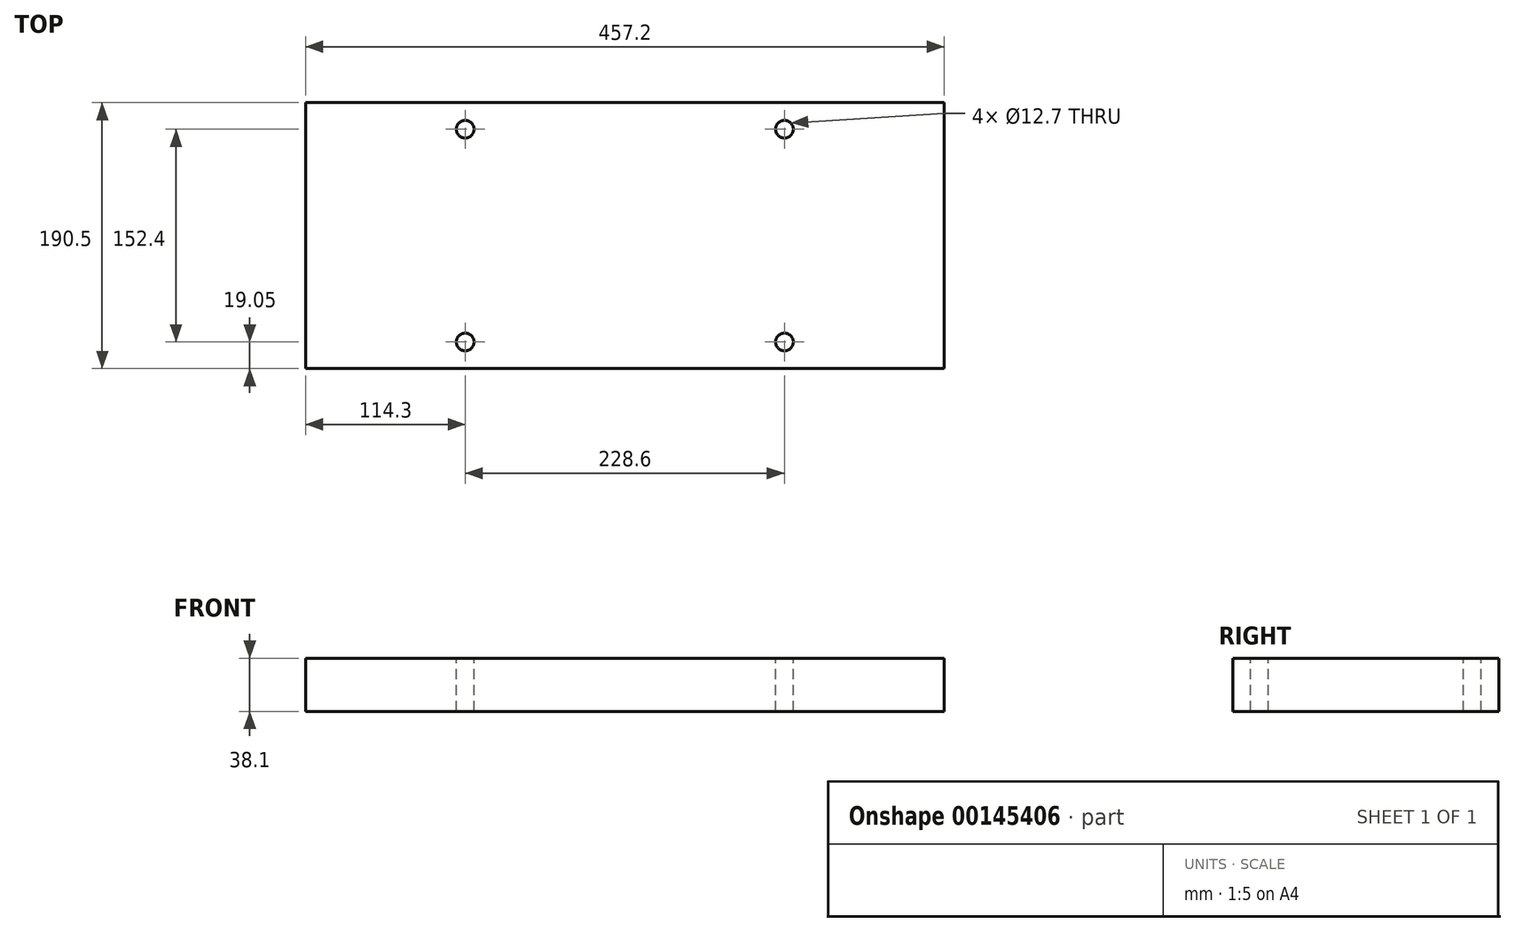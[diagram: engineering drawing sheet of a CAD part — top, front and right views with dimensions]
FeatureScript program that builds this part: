
annotation { "Feature Type Name" : "Feature", "Feature Type Description" : "" }
export const myFeature = defineFeature(function(context is Context, id is Id, definition is map)
    precondition{}
    {
        {
            var Q0;
            Q0=qCreatedBy(makeId("Front.planeOp"),FACE);
            var sketch = newSketch(context, id + "F0", { "sketchPlane" : qUnion([Q0])});
            skLineSegment(sketch, "E0.bottom", {"start": v(-228.6, 19.05) * mm, "end": v(228.6, 19.05) * mm});
            skLineSegment(sketch, "E0.top", {"start": v(-228.6, -19.05) * mm, "end": v(228.6, -19.05) * mm});
            skLineSegment(sketch, "E0.left", {"start": v(-228.6, 19.05) * mm, "end": v(-228.6, -19.05) * mm});
            skLineSegment(sketch, "E0.right", {"start": v(228.6, 19.05) * mm, "end": v(228.6, -19.05) * mm});
            skPoint(sketch, "E0.middle", {"position": v(0, 0) * mm});
            skSolve(sketch);
        }
        {
            var Q0;
            Q0 = qSketchRegion(id + "F0", true);
            extrude(context, id + "F1", {"entities" : qUnion([Q0]), "endBound" : BoundingType.SYMMETRIC, "depth" : 190.5 * mm});
        }
        {
            var Q0;
            Q0=makeQuery(id+"F1.opExtrude","SWEPT_BODY",BODY,{"disambiguationData":[OSD([sQuery(id+"F0.wireOp",EDGE,"E0.bottom"),sQuery(id+"F0.wireOp",EDGE,"E0.top"),sQuery(id+"F0.wireOp",EDGE,"E0.left"),sQuery(id+"F0.wireOp",EDGE,"E0.right")])]});
            transform(context, id + "F2", {"entities" : qUnion([Q0]), "transformType" : TransformType.TRANSLATION_3D, "dx" : 0 * mm, "dy" : 0 * mm, "dz" : 152.4 * mm, "makeCopy" : true});
        }
        {
            var Q0;
            Q0=makeQuery(id+"F2.opPattern","COPY",FACE,{"derivedFrom":makeQuery(id+"F1.opExtrude","SWEPT_FACE",FACE,{"disambiguationData":[OSD([sQuery(id+"F0.wireOp",EDGE,"E0.bottom")])]}),"instanceName":"1"});
            var sketch = newSketch(context, id + "F3", { "sketchPlane" : qUnion([Q0])});
            skPoint(sketch, "E1", {"position": v(114.3, 76.2) * mm});
            skPoint(sketch, "E2", {"position": v(114.3, -76.2) * mm});
            skPoint(sketch, "E3", {"position": v(-114.3, 76.2) * mm});
            skPoint(sketch, "E4", {"position": v(-114.3, -76.2) * mm});
            skSolve(sketch);
        }
        {
            var Q0;
            Q0=sQuery(id+"F3.wireOp",VERTEX,"4ecf7e5d-f871-4dc4-9d11-71fa30564b7e");
            var Q1;
            Q1=sQuery(id+"F3.wireOp",VERTEX,"E3");
            var Q2;
            Q2=makeQuery(id+"F2.opPattern","COPY",BODY,{"derivedFrom":makeQuery(id+"F1.opExtrude","SWEPT_BODY",BODY,{"disambiguationData":[OSD([sQuery(id+"F0.wireOp",EDGE,"E0.bottom"),sQuery(id+"F0.wireOp",EDGE,"E0.top"),sQuery(id+"F0.wireOp",EDGE,"E0.left"),sQuery(id+"F0.wireOp",EDGE,"E0.right")])]}),"instanceName":"1"});
            var Q3;
            Q3=makeQuery(id+"F1.opExtrude","SWEPT_BODY",BODY,{"disambiguationData":[OSD([sQuery(id+"F0.wireOp",EDGE,"E0.bottom"),sQuery(id+"F0.wireOp",EDGE,"E0.top"),sQuery(id+"F0.wireOp",EDGE,"E0.left"),sQuery(id+"F0.wireOp",EDGE,"E0.right")])]});
            hole(context, id + "F4", {"style" : HoleStyle.SIMPLE, "endStyle" : HoleEndStyle.BLIND, "holeDiameter" : 12.7 * mm, "holeDepth" : 609.6 * mm, "locations" : qUnion([Q0, Q1]), "scope" : qUnion([Q2, Q3])});
        }
        {
            var Q0;
            Q0=sQuery(id+"F3.wireOp",VERTEX,"1e3262fc-aa90-4388-9655-f59d1800e4ad");
            var Q1;
            Q1=sQuery(id+"F3.wireOp",VERTEX,"E1");
            var Q2;
            Q2=makeQuery(id+"F2.opPattern","COPY",BODY,{"derivedFrom":makeQuery(id+"F1.opExtrude","SWEPT_BODY",BODY,{"disambiguationData":[OSD([sQuery(id+"F0.wireOp",EDGE,"E0.bottom"),sQuery(id+"F0.wireOp",EDGE,"E0.top"),sQuery(id+"F0.wireOp",EDGE,"E0.left"),sQuery(id+"F0.wireOp",EDGE,"E0.right")])]}),"instanceName":"1"});
            var Q3;
            Q3=makeQuery(id+"F1.opExtrude","SWEPT_BODY",BODY,{"disambiguationData":[OSD([sQuery(id+"F0.wireOp",EDGE,"E0.bottom"),sQuery(id+"F0.wireOp",EDGE,"E0.top"),sQuery(id+"F0.wireOp",EDGE,"E0.left"),sQuery(id+"F0.wireOp",EDGE,"E0.right")])]});
            hole(context, id + "F5", {"style" : HoleStyle.SIMPLE, "endStyle" : HoleEndStyle.BLIND, "holeDiameter" : 12.7 * mm, "holeDepth" : 609.6 * mm, "locations" : qUnion([Q0, Q1]), "scope" : qUnion([Q2, Q3])});
        }
        {
            var Q0;
            Q0=sQuery(id+"F3.wireOp",VERTEX,"c1e96b3d-2616-42c4-94e8-07fb85a00044");
            var Q1;
            Q1=sQuery(id+"F3.wireOp",VERTEX,"E4");
            var Q2;
            Q2=makeQuery(id+"F2.opPattern","COPY",BODY,{"derivedFrom":makeQuery(id+"F1.opExtrude","SWEPT_BODY",BODY,{"disambiguationData":[OSD([sQuery(id+"F0.wireOp",EDGE,"E0.bottom"),sQuery(id+"F0.wireOp",EDGE,"E0.top"),sQuery(id+"F0.wireOp",EDGE,"E0.left"),sQuery(id+"F0.wireOp",EDGE,"E0.right")])]}),"instanceName":"1"});
            var Q3;
            Q3=makeQuery(id+"F1.opExtrude","SWEPT_BODY",BODY,{"disambiguationData":[OSD([sQuery(id+"F0.wireOp",EDGE,"E0.bottom"),sQuery(id+"F0.wireOp",EDGE,"E0.top"),sQuery(id+"F0.wireOp",EDGE,"E0.left"),sQuery(id+"F0.wireOp",EDGE,"E0.right")])]});
            hole(context, id + "F6", {"style" : HoleStyle.SIMPLE, "endStyle" : HoleEndStyle.BLIND, "holeDiameter" : 12.7 * mm, "holeDepth" : 609.6 * mm, "locations" : qUnion([Q0, Q1]), "scope" : qUnion([Q2, Q3])});
        }
        {
            var Q0;
            Q0=sQuery(id+"F3.wireOp",VERTEX,"f6763203-d3ba-4051-b323-57933851997e");
            var Q1;
            Q1=sQuery(id+"F3.wireOp",VERTEX,"E2");
            var Q2;
            Q2=makeQuery(id+"F2.opPattern","COPY",BODY,{"derivedFrom":makeQuery(id+"F1.opExtrude","SWEPT_BODY",BODY,{"disambiguationData":[OSD([sQuery(id+"F0.wireOp",EDGE,"E0.bottom"),sQuery(id+"F0.wireOp",EDGE,"E0.top"),sQuery(id+"F0.wireOp",EDGE,"E0.left"),sQuery(id+"F0.wireOp",EDGE,"E0.right")])]}),"instanceName":"1"});
            var Q3;
            Q3=makeQuery(id+"F1.opExtrude","SWEPT_BODY",BODY,{"disambiguationData":[OSD([sQuery(id+"F0.wireOp",EDGE,"E0.bottom"),sQuery(id+"F0.wireOp",EDGE,"E0.top"),sQuery(id+"F0.wireOp",EDGE,"E0.left"),sQuery(id+"F0.wireOp",EDGE,"E0.right")])]});
            hole(context, id + "F7", {"style" : HoleStyle.SIMPLE, "endStyle" : HoleEndStyle.BLIND, "holeDiameter" : 12.7 * mm, "holeDepth" : 609.6 * mm, "locations" : qUnion([Q0, Q1]), "scope" : qUnion([Q2, Q3])});
        }
        {
            var Q0;
            Q0=makeQuery(id+"F2.opPattern","COPY",BODY,{"derivedFrom":makeQuery(id+"F1.opExtrude","SWEPT_BODY",BODY,{"disambiguationData":[OSD([sQuery(id+"F0.wireOp",EDGE,"E0.bottom"),sQuery(id+"F0.wireOp",EDGE,"E0.top"),sQuery(id+"F0.wireOp",EDGE,"E0.left"),sQuery(id+"F0.wireOp",EDGE,"E0.right")])]}),"instanceName":"1"});
            deleteBodies(context, id + "F8", {"entities" : qUnion([Q0])});
        }
    });
